# Revit family: IS_Conca_T3957_BIM_IT
name_source: partatom
category: Plumbing Fixtures
revit_build: Autodesk Revit 2017 (Build: 20160225_1515(x64)
units: mm (PartAtom-declared; Revit-internal decimal feet)

## family parameters
Always vertical = No
Cut with Voids When Loaded = No
OmniClass Number = 23.45.05.14.21.11
OmniClass Title = Bath/Shower Units
Part Type = Normal
Room Calculation Point = No
Round Connector Dimension = Use Diameter
Shared = No
Work Plane-Based = No

## types (2) — shared parameters
Accessori = https://www.idealstandard.it
Aiuto = https://www.idealstandard.it
Autore = Ideal Standard
BIMobject category = Storage
BIMobject category code = sanitary-storage
BIMobject main category = Sanitary
BIMobject main category code = sanitary
Brand = https://www.idealstandard.it
CodiceABarre = 8014140461753
DescrizioneClassifcazioneUni2015 = Bathroom cabinets
DurataGaranzia = 2
DurataGaranziaProdotti = 2
Forma = Rettangolare
Garanzia = Garanzia Idealstandard
IfcEsportaCome = IfcFurnitureType
InformaziniGaranzia = https://www.idealstandard.it
InformazioniDiProdotto = http://www.idealstandard.it
InformazioniGaranzia = https://www.idealstandard.it
Installation instructions = https://www.idealspec.co.uk
InstruzioniInstallazione = https://www.idealstandard.it
Maniglia = No
Manufacturer = Ideal Standard
Materiale = Ceramics
NominalDepth = 26 mm
NominalHeight = 600 mm  [stored 1.9685 ft]
NominalWidth = 600 mm  [stored 1.9685 ft]
PiattoDoccia = No
Product group = Bathroom_Furniture
Produttore = Ideal Standard
Revisione = 1
RiferimentoClassificazioneUni2015 = Pr_40_30_78_03
Spazio = Interno
Telefono = 800 652 290
TipoEspotazioneIfc = Bathroom cabinets
URL = https://www.ideal-standard.co.uk
Uniclass 2015 Code = Pr_40_30_78_03
Uniclass 2015 Name = Bathroom cabinets
UnitàDurata = Anno
UnitàDurataGaranzia = Anno
UnitàLineare = Milimitre
UnitàMonetaria = €
UnitàSuperficie = Milimitre
UnitàVolume = Litri
Versione = 1
VersioneClassificazioneUni2015 = v1.1
zero-valued in all types: CostoDiSostituzione, DimensioneScarico, LunghezzaNominale, Nominal depth, Nominal height, SeatMaterial, SpessoreDelMateriale, SpilloverLivello, Weight Net (Kg)

## per-type parameters (varying)
| type | AltezzaNominale | Caratteristiche | CodiceArticolo | Colore | Description | Desrizione | Finitura | LarghezzaNominale | Model | ModelloDiRiferimento | Nome | NomeOggettoBim | NumeroDiModello | PesoNetto | ProfonditaNominale |
| Default | 0 mm  [stored 0 ft] | Piano da appogio in gres porcellanato  2000 x 505 x 6 mm  Il gres porcellanato è una ceramica a pasta compatta e dura colorata non porosa un'elevata resistenza alle sollecitazioni meccaniche, agli attacchi chimici, ai graffi e all'abrasione. Si pulisce con estrema facilità. Da abbinare ai mobili sottolavabo senza piano da appoggio.Finitura Marmo calacatta |  | Calacatta marble. | Porcelain stoneware countertop,   2000 x 505 x 6 mm . Compact, hard, non-porous colored ceramic with high resistance to mechanical stress, chemical attack, scratches and abrasion. It is easy to clean. To be combined with vanity units without countertop.Calacatta marble. | Piano da appogio in gres porcellanato  2000 x 505 x 6 mm  Il gres porcellanato è una ceramica a pasta compatta e dura colorata non porosa un'elevata resistenza alle sollecitazioni meccaniche, agli attacchi chimici, ai graffi e all'abrasione. Si pulisce con estrema facilità. Da abbinare ai mobili sottolavabo senza piano da appoggio.Finitura Marmo calacatta | Calacatta marble. | 0 mm  [stored 0 ft] |  |  | BathroomCabinets_Conca__IdealStandard | ISI_IdealStandard_Bathroom Cabinets_Conca_ |  | 0 | 0 mm  [stored 0 ft] |
| T3957BH - MIRROR ROUND 60 Ambience | 26 mm | Specchio rotondo  Ø 600 mm con luce a LED-20 W "Round Ambience" perimetrale. Kit fissaggio incluso 230 V 50 Hz IP44 Classe II | T3957BH | Mirror | Round-MirrorØ 600 mm  with perimeter-Round-MirrorLED-20 W "Round-MirrorAmbience" light. Fixing kit included 230 V 50 Hz IP44 Class II | Specchio rotondo  Ø 600 mm con luce a LED-20 W "Round Ambience" perimetrale. Kit fissaggio incluso 230 V 50 Hz IP44 Classe II | Mirror | 600 mm  [stored 1.9685 ft] | T3957BH | T3957BH | BathroomCabinets_Conca_T3957BH_IdealStandard | ISI_IdealStandard_Bathroom Cabinets_Conca_T3957BH | T3957BH | 4 | 600 mm  [stored 1.9685 ft] |

note: [stored X ft] marks values corroborated as IEEE doubles in the binary element streams (Revit-internal decimal feet)

## geometry (parser evidence)
native form markers: Sweep x2
no freeform markers — native parametric forms only
